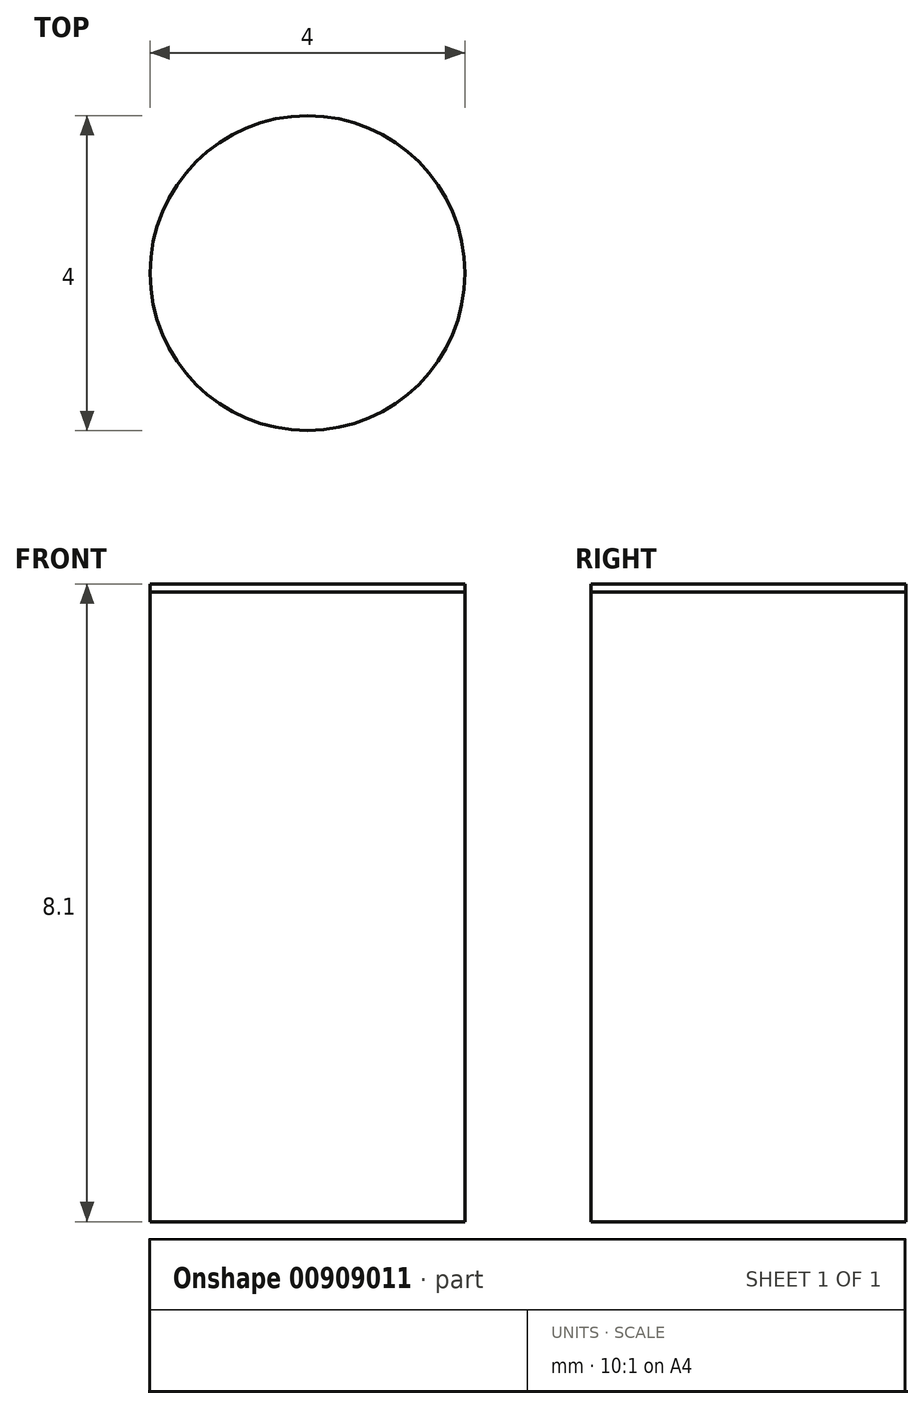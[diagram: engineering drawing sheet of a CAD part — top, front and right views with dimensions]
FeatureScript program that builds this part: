
annotation { "Feature Type Name" : "Feature", "Feature Type Description" : "" }
export const myFeature = defineFeature(function(context is Context, id is Id, definition is map)
    precondition{}
    {
        {
            var Q0;
            Q0=qCreatedBy(makeId("Top.planeOp"),FACE);
            var sketch = newSketch(context, id + "F0", { "sketchPlane" : qUnion([Q0])});
            skCircle(sketch, "E0", {"center": v(0, 0) * mm, "radius": 2 * mm});
            skSolve(sketch);
        }
        {
            var Q0;
            Q0=makeQuery(id+"F0.imprint","IMPRINT",FACE,{"disambiguationData":[TD([[makeQuery(id+"F0.imprint","IMPRINT",EDGE,{"derivedFrom":sQuery(id+"F0.wireOp",EDGE,"E0")}),1.0]])]});
            extrude(context, id + "F1", {"entities" : qUnion([Q0]), "depth" : 8 * mm, "offsetDistance" : 25 * mm});
        }
        {
            var Q0;
            Q0 = qSketchRegion(id + "F0", true);
            extrude(context, id + "F2", {"entities" : qUnion([Q0]), "depth" : 8.1 * mm, "offsetDistance" : 25 * mm});
        }
    });
